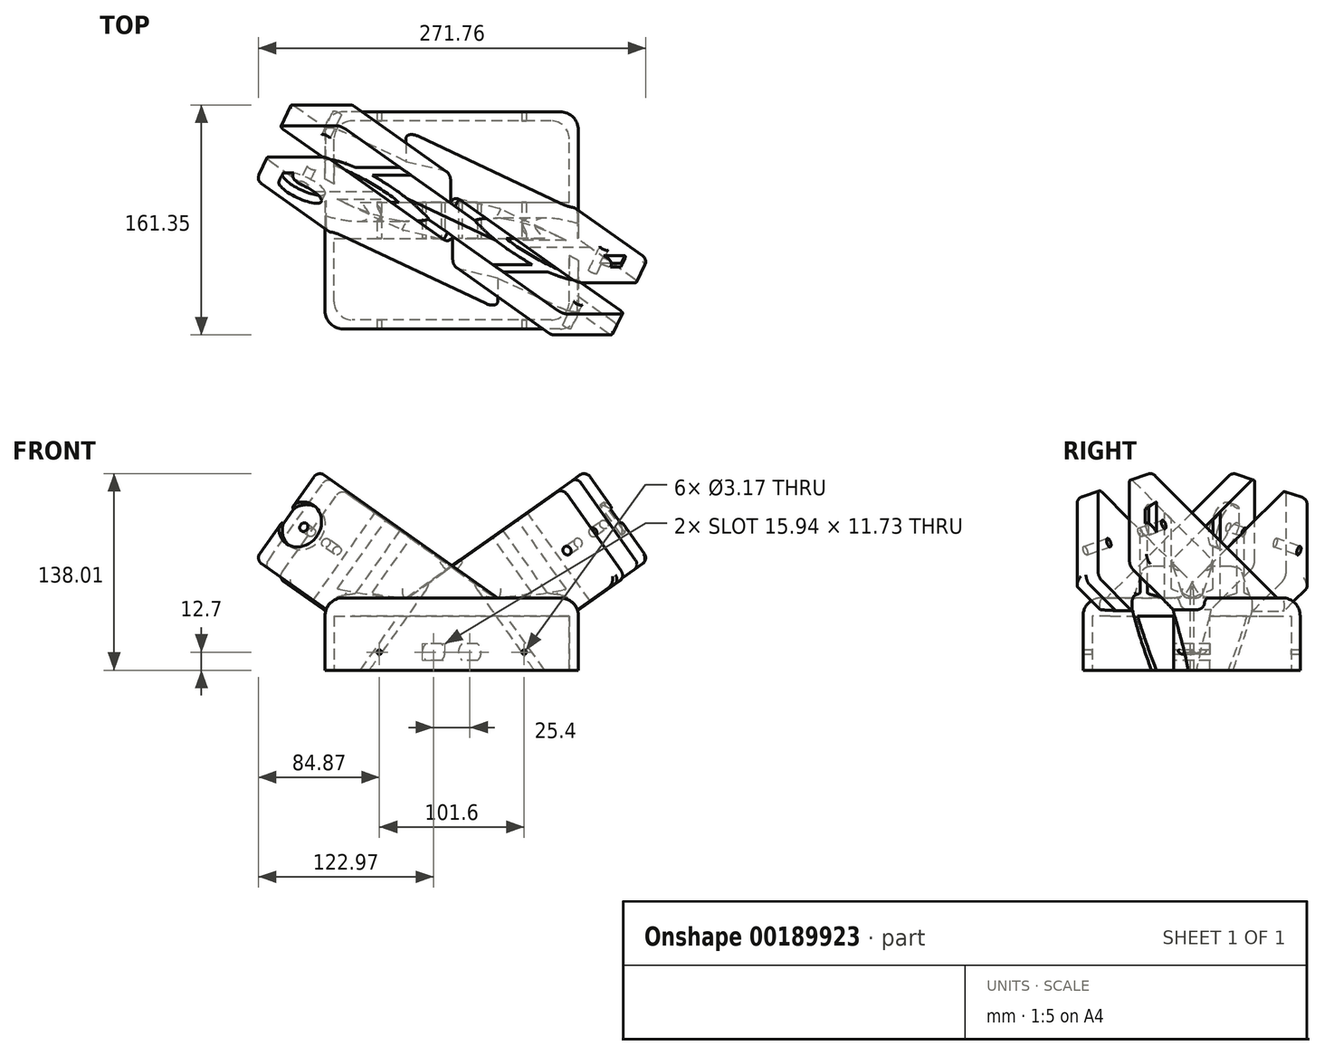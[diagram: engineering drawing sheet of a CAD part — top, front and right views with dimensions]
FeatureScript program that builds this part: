
annotation { "Feature Type Name" : "Feature", "Feature Type Description" : "" }
export const myFeature = defineFeature(function(context is Context, id is Id, definition is map)
    precondition{}
    {
        {
            var Q0;
            Q0=qCreatedBy(makeId("Top.planeOp"),FACE);
            var sketch = newSketch(context, id + "F0", { "sketchPlane" : qUnion([Q0])});
            skLineSegment(sketch, "E0.bottom", {"start": v(76.2, 73.97) * mm, "end": v(-76.2, 73.97) * mm});
            skLineSegment(sketch, "E0.top", {"start": v(76.2, -78.43) * mm, "end": v(-76.2, -78.43) * mm});
            skLineSegment(sketch, "E0.left", {"start": v(88.9, 61.27) * mm, "end": v(88.9, -65.73) * mm});
            skLineSegment(sketch, "E0.right", {"start": v(-88.9, 61.27) * mm, "end": v(-88.9, -65.73) * mm});
            skPoint(sketch, "E0.middle", {"position": v(0, -2.23) * mm});
            skPoint(sketch, "E1.visualSharp", {"position": v(-88.9, 73.97) * mm});
            skArc(sketch, "E1.filletArc", {"start": v(-76.2, 73.97) * mm, "mid": v(-85.18, 70.25) * mm, "end": v(-88.9, 61.27) * mm});
            skPoint(sketch, "E2.visualSharp", {"position": v(88.9, -78.43) * mm});
            skArc(sketch, "E2.filletArc", {"start": v(76.2, -78.43) * mm, "mid": v(85.18, -74.72) * mm, "end": v(88.9, -65.73) * mm});
            skPoint(sketch, "E3.visualSharp", {"position": v(88.9, 73.97) * mm});
            skArc(sketch, "E3.filletArc", {"start": v(88.9, 61.27) * mm, "mid": v(85.18, 70.25) * mm, "end": v(76.2, 73.97) * mm});
            skPoint(sketch, "E4.visualSharp", {"position": v(-88.9, -78.43) * mm});
            skArc(sketch, "E4.filletArc", {"start": v(-88.9, -65.73) * mm, "mid": v(-85.18, -74.72) * mm, "end": v(-76.2, -78.43) * mm});
            skSolve(sketch);
        }
        {
            var Q0;
            Q0 = qSketchRegion(id + "F0", true);
            extrude(context, id + "F1", {"entities" : qUnion([Q0]), "depth" : 50.8 * mm});
        }
        {
            var Q0;
            Q0=makeQuery(id+"F1.opExtrude","CAP_EDGE",EDGE,{"disambiguationData":[OSD([sQuery(id+"F0.wireOp",EDGE,"E0.bottom")])],"isStart":false});
            fillet(context, id + "F2", {"entities" : qUnion([Q0]), "radius" : 12.7 * mm, "tangentPropagation" : true, "allowEdgeOverflow" : false});
        }
        {
            var Q0;
            Q0=makeQuery(id+"F1.opExtrude","CAP_FACE",FACE,{"disambiguationData":[OSD([sQuery(id+"F0.wireOp",EDGE,"E0.bottom"),sQuery(id+"F0.wireOp",EDGE,"E0.top"),sQuery(id+"F0.wireOp",EDGE,"E0.left"),sQuery(id+"F0.wireOp",EDGE,"E0.right"),sQuery(id+"F0.wireOp",EDGE,"E1.filletArc"),sQuery(id+"F0.wireOp",EDGE,"E2.filletArc"),sQuery(id+"F0.wireOp",EDGE,"E3.filletArc"),sQuery(id+"F0.wireOp",EDGE,"E4.filletArc")])],"isStart":false});
            var Q1;
            Q1=makeQuery(id+"F1.opExtrude","SWEPT_FACE",FACE,{"disambiguationData":[OSD([sQuery(id+"F0.wireOp",EDGE,"E0.bottom")])]});
            cPlane(context, id + "F3", {"entities" : qUnion([Q0, Q1]), "cplaneType" : CPlaneType.MID_PLANE, "offset" : 25.4 * mm, "flipAlignment" : true, "width" : 152.4 * mm, "height" : 152.4 * mm});
        }
        {
            var Q0;
            Q0=qCreatedBy(id+"F3.planeOp",FACE);
            var Q1;
            Q1=makeQuery(id+"F1.opExtrude","SWEPT_FACE",FACE,{"disambiguationData":[OSD([sQuery(id+"F0.wireOp",EDGE,"E0.right")])]});
            cPlane(context, id + "F4", {"entities" : qUnion([Q0, Q1]), "cplaneType" : CPlaneType.MID_PLANE, "offset" : 25.4 * mm, "flipAlignment" : true, "width" : 152.4 * mm, "height" : 152.4 * mm});
        }
        {
            var Q0;
            Q0=qCreatedBy(id+"F4.planeOp",FACE);
            var sketch = newSketch(context, id + "F5", { "sketchPlane" : qUnion([Q0])});
            skLineSegment(sketch, "E5.bottom", {"start": v(-6.12, -17.18) * mm, "end": v(12.93, -17.18) * mm});
            skLineSegment(sketch, "E5.top", {"start": v(-6.12, 59.02) * mm, "end": v(12.93, 59.02) * mm});
            skLineSegment(sketch, "E5.left", {"start": v(-6.12, -17.18) * mm, "end": v(-6.12, 59.02) * mm});
            skLineSegment(sketch, "E5.right", {"start": v(12.93, -17.18) * mm, "end": v(12.93, 59.02) * mm});
            skLineSegment(sketch, "E6.bottom", {"start": v(57.38, -16) * mm, "end": v(38.33, -16) * mm});
            skLineSegment(sketch, "E6.top", {"start": v(57.38, 60.2) * mm, "end": v(38.33, 60.2) * mm});
            skLineSegment(sketch, "E6.left", {"start": v(57.38, -16) * mm, "end": v(57.38, 60.2) * mm});
            skLineSegment(sketch, "E6.right", {"start": v(38.33, -16) * mm, "end": v(38.33, 60.2) * mm});
            skSolve(sketch);
        }
        {
            var Q0;
            Q0=makeQuery(id+"F5.imprint","IMPRINT",FACE,{"disambiguationData":[TD([[makeQuery(id+"F5.imprint","IMPRINT",EDGE,{"derivedFrom":sQuery(id+"F5.wireOp",EDGE,"E6.bottom")}),-1.0]])]});
            var Q1;
            Q1=makeQuery(id+"F5.imprint","IMPRINT",FACE,{"disambiguationData":[TD([[makeQuery(id+"F5.imprint","IMPRINT",EDGE,{"derivedFrom":sQuery(id+"F5.wireOp",EDGE,"E5.bottom")}),1.0]])]});
            extrude(context, id + "F6", {"entities" : qUnion([Q0, Q1]), "operationType" : NewBodyOperationType.ADD, "depth" : 25.4 * mm, "hasSecondDirection" : true, "secondDirectionOppositeDirection" : true, "secondDirectionDepth" : 180.34 * mm});
        }
        {
            var Q0;
            Q0=makeQuery(id+"F1.opExtrude","SWEPT_FACE",FACE,{"disambiguationData":[OSD([sQuery(id+"F0.wireOp",EDGE,"E0.top")])]});
            var Q1;
            Q1=makeQuery(id+"F1.opExtrude","CAP_FACE",FACE,{"disambiguationData":[OSD([sQuery(id+"F0.wireOp",EDGE,"E0.bottom"),sQuery(id+"F0.wireOp",EDGE,"E0.top"),sQuery(id+"F0.wireOp",EDGE,"E0.left"),sQuery(id+"F0.wireOp",EDGE,"E0.right"),sQuery(id+"F0.wireOp",EDGE,"E1.filletArc"),sQuery(id+"F0.wireOp",EDGE,"E2.filletArc"),sQuery(id+"F0.wireOp",EDGE,"E3.filletArc"),sQuery(id+"F0.wireOp",EDGE,"E4.filletArc")])],"isStart":false});
            cPlane(context, id + "F7", {"entities" : qUnion([Q0, Q1]), "cplaneType" : CPlaneType.MID_PLANE, "offset" : 25.4 * mm, "flipAlignment" : true, "width" : 152.4 * mm, "height" : 152.4 * mm});
        }
        {
            var Q0;
            Q0=qCreatedBy(id+"F7.planeOp",FACE);
            var Q1;
            Q1=makeQuery(id+"F1.opExtrude","SWEPT_FACE",FACE,{"disambiguationData":[OSD([sQuery(id+"F0.wireOp",EDGE,"E0.left")])]});
            cPlane(context, id + "F8", {"entities" : qUnion([Q0, Q1]), "cplaneType" : CPlaneType.MID_PLANE, "offset" : 25.4 * mm, "flipAlignment" : true, "width" : 152.4 * mm, "height" : 152.4 * mm});
        }
        {
            var Q0;
            Q0=qCreatedBy(id+"F8.planeOp",FACE);
            var sketch = newSketch(context, id + "F9", { "sketchPlane" : qUnion([Q0])});
            skLineSegment(sketch, "E7.bottom", {"start": v(0, -16.82) * mm, "end": v(9.8, -16.82) * mm});
            skLineSegment(sketch, "E7.top", {"start": v(-9.25, 59.38) * mm, "end": v(9.8, 59.38) * mm});
            skLineSegment(sketch, "E7.left", {"start": v(-9.25, -16.23) * mm, "end": v(-9.25, 59.38) * mm});
            skLineSegment(sketch, "E7.right", {"start": v(9.8, -16.82) * mm, "end": v(9.8, 59.38) * mm});
            skLineSegment(sketch, "E8.bottom", {"start": v(35.2, -16.2) * mm, "end": v(54.25, -16.2) * mm});
            skLineSegment(sketch, "E8.top", {"start": v(35.2, 60) * mm, "end": v(54.25, 60) * mm});
            skLineSegment(sketch, "E8.left", {"start": v(35.2, -16.2) * mm, "end": v(35.2, 60) * mm});
            skLineSegment(sketch, "E8.right", {"start": v(54.25, -16.2) * mm, "end": v(54.25, 60) * mm});
            skLineSegment(sketch, "E9", {"start": v(-9.25, -16.23) * mm, "end": v(0, -16.82) * mm});
            skSolve(sketch);
        }
        {
            var Q0;
            Q0 = qSketchRegion(id + "F9", true);
            extrude(context, id + "F10", {"entities" : qUnion([Q0]), "operationType" : NewBodyOperationType.ADD, "depth" : 25.4 * mm, "hasSecondDirection" : true, "secondDirectionOppositeDirection" : true, "secondDirectionDepth" : 180.34 * mm});
        }
        {
            var Q0;
            Q0=makeQuery(id+"F1.opExtrude","SWEPT_FACE",FACE,{"disambiguationData":[OSD([sQuery(id+"F0.wireOp",EDGE,"E0.top")])]});
            var sketch = newSketch(context, id + "F11", { "sketchPlane" : qUnion([Q0])});
            skLineSegment(sketch, "E10.bottom", {"start": v(-76.2, 0) * mm, "end": v(127.6, 0) * mm});
            skLineSegment(sketch, "E10.top", {"start": v(-76.2, -80.49) * mm, "end": v(127.6, -80.49) * mm});
            skLineSegment(sketch, "E10.left", {"start": v(-76.2, 0) * mm, "end": v(-76.2, -80.49) * mm});
            skLineSegment(sketch, "E10.right", {"start": v(127.6, 0) * mm, "end": v(127.6, -80.49) * mm});
            skSolve(sketch);
        }
        {
            var Q0;
            Q0 = qSketchRegion(id + "F11", true);
            extrude(context, id + "F12", {"entities" : qUnion([Q0]), "operationType" : NewBodyOperationType.REMOVE, "endBound" : BoundingType.THROUGH_ALL, "oppositeDirection" : true, "depth" : 25.4 * mm});
        }
        {
            var Q0;
            Q0=makeQuery(id+"F12.boolean.opBoolean","MERGE",FACE,{"derivedFrom":[makeQuery(id+"F1.opExtrude","CAP_FACE",FACE,{"disambiguationData":[OSD([sQuery(id+"F0.wireOp",EDGE,"E0.bottom"),sQuery(id+"F0.wireOp",EDGE,"E0.top"),sQuery(id+"F0.wireOp",EDGE,"E0.left"),sQuery(id+"F0.wireOp",EDGE,"E0.right"),sQuery(id+"F0.wireOp",EDGE,"E1.filletArc"),sQuery(id+"F0.wireOp",EDGE,"E2.filletArc"),sQuery(id+"F0.wireOp",EDGE,"E3.filletArc"),sQuery(id+"F0.wireOp",EDGE,"E4.filletArc")])],"isStart":true}),makeQuery(id+"F12.opExtrude","SWEPT_FACE",FACE,{"disambiguationData":[OSD([sQuery(id+"F11.wireOp",EDGE,"E10.bottom")])]})]});
            var sketch = newSketch(context, id + "F13", { "sketchPlane" : qUnion([Q0])});
            skLineSegment(sketch, "E11.bottom", {"start": v(69.85, 72.08) * mm, "end": v(-69.85, 72.08) * mm});
            skLineSegment(sketch, "E11.top", {"start": v(69.85, -67.62) * mm, "end": v(-69.85, -67.62) * mm});
            skLineSegment(sketch, "E11.left", {"start": v(82.55, 59.38) * mm, "end": v(82.55, -54.92) * mm});
            skLineSegment(sketch, "E11.right", {"start": v(-82.55, 59.38) * mm, "end": v(-82.55, -54.92) * mm});
            skPoint(sketch, "E11.middle", {"position": v(0, 0) * mm});
            skPoint(sketch, "E12.visualSharp", {"position": v(-82.55, 72.08) * mm});
            skArc(sketch, "E12.filletArc", {"start": v(-69.85, 72.08) * mm, "mid": v(-78.83, 68.37) * mm, "end": v(-82.55, 59.38) * mm});
            skPoint(sketch, "E13.visualSharp", {"position": v(-82.55, -67.62) * mm});
            skArc(sketch, "E13.filletArc", {"start": v(-82.55, -54.92) * mm, "mid": v(-78.83, -63.9) * mm, "end": v(-69.85, -67.62) * mm});
            skPoint(sketch, "E14.visualSharp", {"position": v(82.55, -67.62) * mm});
            skArc(sketch, "E14.filletArc", {"start": v(69.85, -67.62) * mm, "mid": v(78.83, -63.9) * mm, "end": v(82.55, -54.92) * mm});
            skPoint(sketch, "E15.visualSharp", {"position": v(82.55, 72.08) * mm});
            skArc(sketch, "E15.filletArc", {"start": v(82.55, 59.38) * mm, "mid": v(78.83, 68.37) * mm, "end": v(69.85, 72.08) * mm});
            skLineSegment(sketch, "E16.bottom", {"start": v(-82.55, -10.47) * mm, "end": v(82.55, -10.47) * mm});
            skLineSegment(sketch, "E16.top", {"start": v(-82.55, 14.93) * mm, "end": v(82.55, 14.93) * mm});
            skLineSegment(sketch, "E16.left", {"start": v(-82.55, -10.47) * mm, "end": v(-82.55, 14.93) * mm});
            skLineSegment(sketch, "E16.right", {"start": v(82.55, -10.47) * mm, "end": v(82.55, 14.93) * mm});
            skSolve(sketch);
        }
        {
            var Q0;
            Q0=makeQuery(id+"F13.imprint","IMPRINT",FACE,{"disambiguationData":[TD([[makeQuery(id+"F13.imprint","IMPRINT",EDGE,{"derivedFrom":sQuery(id+"F13.wireOp",EDGE,"E11.bottom")}),1.0]])]});
            var Q1;
            Q1=makeQuery(id+"F13.imprint","IMPRINT",FACE,{"disambiguationData":[TD([[makeQuery(id+"F13.imprint","IMPRINT",EDGE,{"derivedFrom":sQuery(id+"F13.wireOp",EDGE,"E11.top")}),-1.0]])]});
            extrude(context, id + "F14", {"entities" : qUnion([Q0, Q1]), "operationType" : NewBodyOperationType.REMOVE, "oppositeDirection" : true, "depth" : 38.1 * mm});
        }
        {
            var Q0;
            Q0=makeQuery(id+"F10.opExtrude","CAP_EDGE",EDGE,{"disambiguationData":[OSD([sQuery(id+"F9.wireOp",EDGE,"E7.bottom")])],"isStart":false});
            var Q1;
            Q1=makeQuery(id+"F10.opExtrude","CAP_EDGE",EDGE,{"disambiguationData":[OSD([sQuery(id+"F9.wireOp",EDGE,"E7.top")])],"isStart":false});
            var Q2;
            Q2=makeQuery(id+"F10.opExtrude","CAP_EDGE",EDGE,{"disambiguationData":[OSD([sQuery(id+"F9.wireOp",EDGE,"E8.top")])],"isStart":false});
            var Q3;
            Q3=makeQuery(id+"F10.opExtrude","CAP_EDGE",EDGE,{"disambiguationData":[OSD([sQuery(id+"F9.wireOp",EDGE,"E8.bottom")])],"isStart":false});
            var Q4;
            Q4=makeQuery(id+"F10.opExtrude","CAP_EDGE",EDGE,{"disambiguationData":[OSD([sQuery(id+"F9.wireOp",EDGE,"E9")])],"isStart":false});
            var Q5;
            Q5=makeQuery(id+"F10.opExtrude","CAP_EDGE",EDGE,{"disambiguationData":[OSD([sQuery(id+"F9.wireOp",EDGE,"E7.left")])],"isStart":false});
            var Q6;
            Q6=makeQuery(id+"F10.opExtrude","CAP_EDGE",EDGE,{"disambiguationData":[OSD([sQuery(id+"F9.wireOp",EDGE,"E8.right")])],"isStart":false});
            var Q7;
            Q7=makeQuery(id+"F6.opExtrude","CAP_EDGE",EDGE,{"disambiguationData":[OSD([sQuery(id+"F5.wireOp",EDGE,"E6.left")])],"isStart":false});
            var Q8;
            Q8=makeQuery(id+"F6.opExtrude","CAP_EDGE",EDGE,{"disambiguationData":[OSD([sQuery(id+"F5.wireOp",EDGE,"E6.bottom")])],"isStart":false});
            var Q9;
            Q9=makeQuery(id+"F6.opExtrude","CAP_EDGE",EDGE,{"disambiguationData":[OSD([sQuery(id+"F5.wireOp",EDGE,"E6.top")])],"isStart":false});
            var Q10;
            Q10=makeQuery(id+"F6.opExtrude","CAP_EDGE",EDGE,{"disambiguationData":[OSD([sQuery(id+"F5.wireOp",EDGE,"E5.bottom")])],"isStart":false});
            var Q11;
            Q11=makeQuery(id+"F6.opExtrude","CAP_EDGE",EDGE,{"disambiguationData":[OSD([sQuery(id+"F5.wireOp",EDGE,"E5.left")])],"isStart":false});
            var Q12;
            Q12=makeQuery(id+"F6.opExtrude","CAP_EDGE",EDGE,{"disambiguationData":[OSD([sQuery(id+"F5.wireOp",EDGE,"E5.top")])],"isStart":false});
            var Q13;
            Q13=makeQuery(id+"F6.opExtrude","SWEPT_EDGE",EDGE,{"disambiguationData":[OSD([sQuery(id+"F5.wireOp",EDGE,"E5.top"),sQuery(id+"F5.wireOp",EDGE,"E5.left")])]});
            var Q14;
            Q14=makeQuery(id+"F6.opExtrude","SWEPT_EDGE",EDGE,{"disambiguationData":[OSD([sQuery(id+"F5.wireOp",EDGE,"E6.top"),sQuery(id+"F5.wireOp",EDGE,"E6.left")])]});
            var Q15;
            {var subQ0=sQuery(id+"F5.wireOp",EDGE,"E6.bottom");var subQ1=sQuery(id+"F5.wireOp",EDGE,"E6.left");Q15=makeQuery(id+"F6.boolean.opBoolean","SPLIT",EDGE,{"disambiguationData":[TD([makeQuery(id+"F6.opExtrude","CAP_FACE",FACE,{"disambiguationData":[OSD([subQ0,sQuery(id+"F5.wireOp",EDGE,"E6.top"),subQ1,sQuery(id+"F5.wireOp",EDGE,"E6.right")])],"isStart":false})])],"derivedFrom":makeQuery(id+"F6.opExtrude","SWEPT_EDGE",EDGE,{"disambiguationData":[OSD([subQ0,subQ1])]})});}
            var Q16;
            {var subQ0=sQuery(id+"F5.wireOp",EDGE,"E5.left");var subQ1=sQuery(id+"F5.wireOp",EDGE,"E5.bottom");Q16=makeQuery(id+"F6.boolean.opBoolean","SPLIT",EDGE,{"disambiguationData":[TD([makeQuery(id+"F2.opFillet","BLEND_FACE",FACE,{"disambiguationData":[OSD([sQuery(id+"F0.wireOp",EDGE,"E0.bottom")])]})])],"derivedFrom":makeQuery(id+"F6.opExtrude","SWEPT_EDGE",EDGE,{"disambiguationData":[OSD([subQ1,subQ0])]})});}
            var Q17;
            Q17=makeQuery(id+"F10.opExtrude","SWEPT_EDGE",EDGE,{"disambiguationData":[OSD([sQuery(id+"F9.wireOp",EDGE,"E8.top"),sQuery(id+"F9.wireOp",EDGE,"E8.right")])]});
            var Q18;
            Q18=makeQuery(id+"F10.opExtrude","SWEPT_EDGE",EDGE,{"disambiguationData":[OSD([sQuery(id+"F9.wireOp",EDGE,"E7.top"),sQuery(id+"F9.wireOp",EDGE,"E7.left")])]});
            var Q19;
            {var subQ0=sQuery(id+"F9.wireOp",EDGE,"E7.left");var subQ1=sQuery(id+"F9.wireOp",EDGE,"E9");Q19=makeQuery(id+"F10.boolean.opBoolean","SPLIT",EDGE,{"disambiguationData":[TD([makeQuery(id+"F2.opFillet","BLEND_FACE",FACE,{"disambiguationData":[OSD([sQuery(id+"F0.wireOp",EDGE,"E0.top")])]})])],"derivedFrom":makeQuery(id+"F10.opExtrude","SWEPT_EDGE",EDGE,{"disambiguationData":[OSD([subQ0,subQ1])]})});}
            var Q20;
            {var subQ0=sQuery(id+"F9.wireOp",EDGE,"E8.bottom");var subQ1=sQuery(id+"F9.wireOp",EDGE,"E8.right");Q20=makeQuery(id+"F10.boolean.opBoolean","SPLIT",EDGE,{"disambiguationData":[TD([makeQuery(id+"F10.opExtrude","CAP_FACE",FACE,{"disambiguationData":[OSD([subQ0,sQuery(id+"F9.wireOp",EDGE,"E8.top"),sQuery(id+"F9.wireOp",EDGE,"E8.left"),subQ1])],"isStart":false})])],"derivedFrom":makeQuery(id+"F10.opExtrude","SWEPT_EDGE",EDGE,{"disambiguationData":[OSD([subQ0,subQ1])]})});}
            fillet(context, id + "F15", {"entities" : qUnion([Q0, Q1, Q2, Q3, Q4, Q5, Q6, Q7, Q8, Q9, Q10, Q11, Q12, Q13, Q14, Q15, Q16, Q17, Q18, Q19, Q20]), "radius" : 5.08 * mm, "tangentPropagation" : true, "allowEdgeOverflow" : false});
        }
        {
            var Q0;
            {var subQ1=sQuery(id+"F9.wireOp",EDGE,"E8.right");var subQ2=sQuery(id+"F9.wireOp",EDGE,"E8.top");Q0=makeQuery(id+"F10.boolean.opBoolean","SPLIT",FACE,{"disambiguationData":[TD([makeQuery(id+"F10.opExtrude","SWEPT_FACE",FACE,{"disambiguationData":[OSD([subQ2])]})])],"derivedFrom":makeQuery(id+"F10.opExtrude","SWEPT_FACE",FACE,{"disambiguationData":[OSD([subQ1])]})});}
            var sketch = newSketch(context, id + "F16", { "sketchPlane" : qUnion([Q0])});
            skCircle(sketch, "E17", {"center": v(-92.77, 104) * mm, "radius": 3.18 * mm});
            skLineSegment(sketch, "E18", {"start": v(-100.64, 110.44) * mm, "end": v(-61.64, 78.6) * mm, "construction": true});
            skSolve(sketch);
        }
        {
            var Q0;
            Q0 = qSketchRegion(id + "F16", true);
            extrude(context, id + "F17", {"entities" : qUnion([Q0]), "operationType" : NewBodyOperationType.REMOVE, "endBound" : BoundingType.THROUGH_ALL, "oppositeDirection" : true, "depth" : 25.4 * mm});
        }
        {
            var Q0;
            {var subQ1=sQuery(id+"F5.wireOp",EDGE,"E6.left");var subQ2=sQuery(id+"F5.wireOp",EDGE,"E6.top");Q0=makeQuery(id+"F6.boolean.opBoolean","SPLIT",FACE,{"disambiguationData":[TD([makeQuery(id+"F6.opExtrude","SWEPT_FACE",FACE,{"disambiguationData":[OSD([subQ2])]})])],"derivedFrom":makeQuery(id+"F6.opExtrude","SWEPT_FACE",FACE,{"disambiguationData":[OSD([subQ1])]})});}
            var sketch = newSketch(context, id + "F18", { "sketchPlane" : qUnion([Q0])});
            skLineSegment(sketch, "E19", {"start": v(-98.78, 109.18) * mm, "end": v(-95.73, 106.7) * mm, "construction": true});
            skCircle(sketch, "E20", {"center": v(-90.9, 102.76) * mm, "radius": 3.18 * mm});
            skSolve(sketch);
        }
        {
            var Q0;
            Q0=makeQuery(id+"F18.imprint","IMPRINT",FACE,{"disambiguationData":[TD([[makeQuery(id+"F18.imprint","IMPRINT",EDGE,{"derivedFrom":sQuery(id+"F18.wireOp",EDGE,"E20")}),1.0]])]});
            extrude(context, id + "F19", {"entities" : qUnion([Q0]), "operationType" : NewBodyOperationType.REMOVE, "endBound" : BoundingType.THROUGH_ALL, "oppositeDirection" : true, "depth" : 25.4 * mm});
        }
        {
            var Q0;
            Q0=makeQuery(id+"F6.boolean.opBoolean","INTERSECT",EDGE,{"derivedFrom":[makeQuery(id+"F1.opExtrude","CAP_FACE",FACE,{"disambiguationData":[OSD([sQuery(id+"F0.wireOp",EDGE,"E0.bottom"),sQuery(id+"F0.wireOp",EDGE,"E0.top"),sQuery(id+"F0.wireOp",EDGE,"E0.left"),sQuery(id+"F0.wireOp",EDGE,"E0.right"),sQuery(id+"F0.wireOp",EDGE,"E1.filletArc"),sQuery(id+"F0.wireOp",EDGE,"E2.filletArc"),sQuery(id+"F0.wireOp",EDGE,"E3.filletArc"),sQuery(id+"F0.wireOp",EDGE,"E4.filletArc")])],"isStart":false}),makeQuery(id+"F6.opExtrude","SWEPT_FACE",FACE,{"disambiguationData":[OSD([sQuery(id+"F5.wireOp",EDGE,"E5.right")])]})]});
            var Q1;
            Q1=makeQuery(id+"F6.boolean.opBoolean","INTERSECT",EDGE,{"derivedFrom":[makeQuery(id+"F1.opExtrude","CAP_FACE",FACE,{"disambiguationData":[OSD([sQuery(id+"F0.wireOp",EDGE,"E0.bottom"),sQuery(id+"F0.wireOp",EDGE,"E0.top"),sQuery(id+"F0.wireOp",EDGE,"E0.left"),sQuery(id+"F0.wireOp",EDGE,"E0.right"),sQuery(id+"F0.wireOp",EDGE,"E1.filletArc"),sQuery(id+"F0.wireOp",EDGE,"E2.filletArc"),sQuery(id+"F0.wireOp",EDGE,"E3.filletArc"),sQuery(id+"F0.wireOp",EDGE,"E4.filletArc")])],"isStart":false}),makeQuery(id+"F6.opExtrude","SWEPT_FACE",FACE,{"disambiguationData":[OSD([sQuery(id+"F5.wireOp",EDGE,"E6.right")])]})]});
            fillet(context, id + "F20", {"entities" : qUnion([Q0, Q1]), "radius" : 5.08 * mm, "tangentPropagation" : true, "allowEdgeOverflow" : false});
        }
        {
            var Q0;
            Q0=makeQuery(id+"F10.boolean.opBoolean","INTERSECT",EDGE,{"derivedFrom":[makeQuery(id+"F1.opExtrude","CAP_FACE",FACE,{"disambiguationData":[OSD([sQuery(id+"F0.wireOp",EDGE,"E0.bottom"),sQuery(id+"F0.wireOp",EDGE,"E0.top"),sQuery(id+"F0.wireOp",EDGE,"E0.left"),sQuery(id+"F0.wireOp",EDGE,"E0.right"),sQuery(id+"F0.wireOp",EDGE,"E1.filletArc"),sQuery(id+"F0.wireOp",EDGE,"E2.filletArc"),sQuery(id+"F0.wireOp",EDGE,"E3.filletArc"),sQuery(id+"F0.wireOp",EDGE,"E4.filletArc")])],"isStart":false}),makeQuery(id+"F10.opExtrude","SWEPT_FACE",FACE,{"disambiguationData":[OSD([sQuery(id+"F9.wireOp",EDGE,"E7.right")])]})]});
            var Q1;
            Q1=makeQuery(id+"F10.boolean.opBoolean","INTERSECT",EDGE,{"derivedFrom":[makeQuery(id+"F1.opExtrude","CAP_FACE",FACE,{"disambiguationData":[OSD([sQuery(id+"F0.wireOp",EDGE,"E0.bottom"),sQuery(id+"F0.wireOp",EDGE,"E0.top"),sQuery(id+"F0.wireOp",EDGE,"E0.left"),sQuery(id+"F0.wireOp",EDGE,"E0.right"),sQuery(id+"F0.wireOp",EDGE,"E1.filletArc"),sQuery(id+"F0.wireOp",EDGE,"E2.filletArc"),sQuery(id+"F0.wireOp",EDGE,"E3.filletArc"),sQuery(id+"F0.wireOp",EDGE,"E4.filletArc")])],"isStart":false}),makeQuery(id+"F10.opExtrude","SWEPT_FACE",FACE,{"disambiguationData":[OSD([sQuery(id+"F9.wireOp",EDGE,"E8.left")])]})]});
            fillet(context, id + "F21", {"entities" : qUnion([Q0, Q1]), "radius" : 5.08 * mm, "tangentPropagation" : true, "allowEdgeOverflow" : false});
        }
        {
            var Q0;
            Q0=makeQuery(id+"F6.boolean.opBoolean","INTERSECT",EDGE,{"derivedFrom":[makeQuery(id+"F1.opExtrude","CAP_FACE",FACE,{"disambiguationData":[OSD([sQuery(id+"F0.wireOp",EDGE,"E0.bottom"),sQuery(id+"F0.wireOp",EDGE,"E0.top"),sQuery(id+"F0.wireOp",EDGE,"E0.left"),sQuery(id+"F0.wireOp",EDGE,"E0.right"),sQuery(id+"F0.wireOp",EDGE,"E1.filletArc"),sQuery(id+"F0.wireOp",EDGE,"E2.filletArc"),sQuery(id+"F0.wireOp",EDGE,"E3.filletArc"),sQuery(id+"F0.wireOp",EDGE,"E4.filletArc")])],"isStart":false}),makeQuery(id+"F6.opExtrude","SWEPT_FACE",FACE,{"disambiguationData":[OSD([sQuery(id+"F5.wireOp",EDGE,"E5.top")])]})]});
            var Q1;
            Q1=makeQuery(id+"F10.boolean.opBoolean","INTERSECT",EDGE,{"derivedFrom":[makeQuery(id+"F1.opExtrude","CAP_FACE",FACE,{"disambiguationData":[OSD([sQuery(id+"F0.wireOp",EDGE,"E0.bottom"),sQuery(id+"F0.wireOp",EDGE,"E0.top"),sQuery(id+"F0.wireOp",EDGE,"E0.left"),sQuery(id+"F0.wireOp",EDGE,"E0.right"),sQuery(id+"F0.wireOp",EDGE,"E1.filletArc"),sQuery(id+"F0.wireOp",EDGE,"E2.filletArc"),sQuery(id+"F0.wireOp",EDGE,"E3.filletArc"),sQuery(id+"F0.wireOp",EDGE,"E4.filletArc")])],"isStart":false}),makeQuery(id+"F10.opExtrude","SWEPT_FACE",FACE,{"disambiguationData":[OSD([sQuery(id+"F9.wireOp",EDGE,"E7.top")])]})]});
            fillet(context, id + "F22", {"entities" : qUnion([Q0, Q1]), "radius" : 5.08 * mm, "tangentPropagation" : true, "allowEdgeOverflow" : false});
        }
        {
            var Q0;
            Q0=makeQuery(id+"F1.opExtrude","SWEPT_FACE",FACE,{"disambiguationData":[OSD([sQuery(id+"F0.wireOp",EDGE,"E0.top")])]});
            var sketch = newSketch(context, id + "F23", { "sketchPlane" : qUnion([Q0])});
            skCircle(sketch, "E21", {"center": v(-50.8, 12.7) * mm, "radius": 1.59 * mm});
            skCircle(sketch, "E22", {"center": v(50.8, 12.7) * mm, "radius": 1.59 * mm});
            skSolve(sketch);
        }
        {
            var Q0;
            Q0 = qSketchRegion(id + "F23", true);
            extrude(context, id + "F24", {"entities" : qUnion([Q0]), "operationType" : NewBodyOperationType.REMOVE, "endBound" : BoundingType.THROUGH_ALL, "oppositeDirection" : true, "depth" : 25.4 * mm});
        }
        {
            var Q0;
            Q0=makeQuery(id+"F14.boolean.opBoolean","COPY",FACE,{"derivedFrom":makeQuery(id+"F14.opExtrude","SWEPT_FACE",FACE,{"disambiguationData":[OSD([sQuery(id+"F13.wireOp",EDGE,"E16.top")])]})});
            cPlane(context, id + "F25", {"entities" : qUnion([Q0]), "cplaneType" : CPlaneType.OFFSET, "offset" : 25.4 * mm, "width" : 152.4 * mm, "height" : 152.4 * mm});
        }
        {
            var Q0;
            Q0=qCreatedBy(id+"F25.planeOp",FACE);
            var sketch = newSketch(context, id + "F26", { "sketchPlane" : qUnion([Q0])});
            skArc(sketch, "E23", {"start": v(-7.3, 6.83) * mm, "mid": v(-4.73, 12.7) * mm, "end": v(-7.3, 18.57) * mm});
            skLineSegment(sketch, "E24", {"start": v(-18.1, 18.57) * mm, "end": v(-7.3, 18.57) * mm});
            skLineSegment(sketch, "E25", {"start": v(-18.1, 6.83) * mm, "end": v(-7.3, 6.83) * mm});
            skArc(sketch, "E26.trimOffspring", {"start": v(-18.1, 18.57) * mm, "mid": v(-20.67, 12.7) * mm, "end": v(-18.1, 6.83) * mm});
            skArc(sketch, "E27", {"start": v(18.1, 6.83) * mm, "mid": v(20.67, 12.7) * mm, "end": v(18.1, 18.57) * mm});
            skLineSegment(sketch, "E28", {"start": v(7.3, 18.57) * mm, "end": v(18.1, 18.57) * mm});
            skLineSegment(sketch, "E29", {"start": v(7.3, 6.83) * mm, "end": v(18.1, 6.83) * mm});
            skArc(sketch, "E30.trimOffspring", {"start": v(7.3, 18.57) * mm, "mid": v(4.73, 12.7) * mm, "end": v(7.3, 6.83) * mm});
            skSolve(sketch);
        }
        {
            var Q0;
            {var subQ0=sQuery(id+"F26.wireOp",EDGE,"E24");Q0=makeQuery(id+"F26.imprint","IMPRINT",FACE,{"disambiguationData":[TD([[makeQuery(id+"F26.imprint","IMPRINT",EDGE,{"derivedFrom":subQ0}),-1.0]])]});}
            var Q1;
            Q1=makeQuery(id+"F26.imprint","IMPRINT",FACE,{"disambiguationData":[TD([[makeQuery(id+"F26.imprint","IMPRINT",EDGE,{"derivedFrom":sQuery(id+"F26.wireOp",EDGE,"E27")}),1.0]])]});
            var Q2;
            Q2=makeQuery(id+"F14.boolean.opBoolean","COPY",FACE,{"derivedFrom":makeQuery(id+"F14.opExtrude","SWEPT_FACE",FACE,{"disambiguationData":[OSD([sQuery(id+"F13.wireOp",EDGE,"E11.top")])]})});
            extrude(context, id + "F27", {"entities" : qUnion([Q0, Q1]), "operationType" : NewBodyOperationType.REMOVE, "endBound" : BoundingType.UP_TO_SURFACE, "oppositeDirection" : true, "endBoundEntityFace" : qUnion([Q2]), "depth" : 25.4 * mm});
        }
        {
            var Q0;
            Q0=makeQuery(id+"F22.opFillet","SPLIT",FACE,{"disambiguationData":[OD(0.0)],"derivedFrom":makeQuery(id+"F10.opExtrude","SWEPT_FACE",FACE,{"disambiguationData":[OSD([sQuery(id+"F9.wireOp",EDGE,"E7.top")])]})});
            var Q1;
            Q1=makeQuery(id+"F10.opExtrude","SWEPT_FACE",FACE,{"disambiguationData":[OSD([sQuery(id+"F9.wireOp",EDGE,"E8.top")])]});
            cPlane(context, id + "F28", {"entities" : qUnion([Q0, Q1]), "cplaneType" : CPlaneType.MID_PLANE, "offset" : 25.4 * mm, "width" : 152.4 * mm, "height" : 152.4 * mm});
        }
        {
            var Q0;
            Q0=qCreatedBy(id+"F28.planeOp",FACE);
            var sketch = newSketch(context, id + "F29", { "sketchPlane" : qUnion([Q0])});
            skLineSegment(sketch, "E31", {"start": v(149.45, -45.64) * mm, "end": v(47.98, 12.94) * mm, "construction": true});
            skLineSegment(sketch, "E32", {"start": v(98.71, -16.35) * mm, "end": v(86.01, -38.35) * mm, "construction": true});
            skEllipse(sketch, "E33", {"center": v(92.36, -27.35) * mm, "majorRadius": 50.8 * mm, "minorRadius": 12.7 * mm, "majorAxis": v(0.88, -0.48)});
            skSolve(sketch);
        }
        {
            var Q0;
            Q0 = qSketchRegion(id + "F29", true);
            extrude(context, id + "F30", {"entities" : qUnion([Q0]), "operationType" : NewBodyOperationType.REMOVE, "endBound" : BoundingType.THROUGH_ALL, "oppositeDirection" : true, "depth" : 25.4 * mm});
        }
        {
            var Q0;
            Q0=makeQuery(id+"F22.opFillet","SPLIT",FACE,{"disambiguationData":[OD(0.0)],"derivedFrom":makeQuery(id+"F6.opExtrude","SWEPT_FACE",FACE,{"disambiguationData":[OSD([sQuery(id+"F5.wireOp",EDGE,"E5.top")])]})});
            var Q1;
            Q1=makeQuery(id+"F6.opExtrude","SWEPT_FACE",FACE,{"disambiguationData":[OSD([sQuery(id+"F5.wireOp",EDGE,"E6.top")])]});
            cPlane(context, id + "F31", {"entities" : qUnion([Q0, Q1]), "cplaneType" : CPlaneType.MID_PLANE, "offset" : 25.4 * mm, "width" : 152.4 * mm, "height" : 152.4 * mm});
        }
        {
            var Q0;
            Q0=qCreatedBy(id+"F31.planeOp",FACE);
            var sketch = newSketch(context, id + "F32", { "sketchPlane" : qUnion([Q0])});
            skLineSegment(sketch, "E34", {"start": v(-149.16, 41.85) * mm, "end": v(-48.24, -16.41) * mm, "construction": true});
            skLineSegment(sketch, "E35", {"start": v(-98.7, 12.72) * mm, "end": v(-86, 34.72) * mm, "construction": true});
            skEllipse(sketch, "E36", {"center": v(-92.35, 23.72) * mm, "majorRadius": 50.8 * mm, "minorRadius": 12.7 * mm, "majorAxis": v(-0.88, 0.48)});
            skSolve(sketch);
        }
        {
            var Q0;
            Q0 = qSketchRegion(id + "F32", true);
            extrude(context, id + "F33", {"entities" : qUnion([Q0]), "operationType" : NewBodyOperationType.REMOVE, "endBound" : BoundingType.THROUGH_ALL, "oppositeDirection" : true, "depth" : 25.4 * mm});
        }
        {
            var Q0;
            {var subQ0=sQuery(id+"F9.wireOp",EDGE,"E8.right");var subQ3=sQuery(id+"F0.wireOp",EDGE,"E0.left");Q0=makeQuery(id+"F10.boolean.opBoolean","SPLIT",FACE,{"disambiguationData":[TD([makeQuery(id+"F2.opFillet","BLEND_FACE",FACE,{"disambiguationData":[OSD([subQ3])]})])],"derivedFrom":makeQuery(id+"F10.opExtrude","SWEPT_FACE",FACE,{"disambiguationData":[OSD([subQ0])]})});}
            var sketch = newSketch(context, id + "F34", { "sketchPlane" : qUnion([Q0])});
            skCircle(sketch, "E37", {"center": v(-92.77, 104) * mm, "radius": 16.51 * mm});
            skSolve(sketch);
        }
        {
            var Q0;
            Q0=makeQuery(id+"F34.imprint","IMPRINT",FACE,{"disambiguationData":[TD([[makeQuery(id+"F34.imprint","IMPRINT",EDGE,{"derivedFrom":makeQuery(id+"F17.boolean.opBoolean","COPY",EDGE,{"derivedFrom":makeQuery(id+"F17.opExtrude","CAP_EDGE",EDGE,{"disambiguationData":[OSD([sQuery(id+"F16.wireOp",EDGE,"E17")])],"isStart":true})})}),-1.0]])]});
            var Q1;
            {var subQ0=sQuery(id+"F34.wireOp",EDGE,"E37");var subQ1=sQuery(id+"F9.wireOp",EDGE,"E8.right");var subQ4=sQuery(id+"F0.wireOp",EDGE,"E0.left");var subQ5=makeQuery(id+"F15.opFillet","BLEND_EDGE",EDGE,{"blendedFrom":[makeQuery(id+"F10.opExtrude","CAP_EDGE",EDGE,{"disambiguationData":[OSD([subQ1])],"isStart":false}),makeQuery(id+"F10.boolean.opBoolean","SPLIT",FACE,{"disambiguationData":[TD([makeQuery(id+"F2.opFillet","BLEND_FACE",FACE,{"disambiguationData":[OSD([subQ4])]})])],"derivedFrom":makeQuery(id+"F10.opExtrude","SWEPT_FACE",FACE,{"disambiguationData":[OSD([subQ1])]})})],"blendedInto":[makeQuery(id+"F10.boolean.opBoolean","SPLIT",FACE,{"disambiguationData":[TD([makeQuery(id+"F2.opFillet","BLEND_FACE",FACE,{"disambiguationData":[OSD([subQ4])]})])],"derivedFrom":makeQuery(id+"F10.opExtrude","SWEPT_FACE",FACE,{"disambiguationData":[OSD([subQ1])]})})]});var subQ6=makeQuery(id+"F34.imprint","INTERSECT",VERTEX,{"disambiguationData":[OD(0.0)],"derivedFrom":[subQ5,subQ0]});Q1=makeQuery(id+"F34.imprint","IMPRINT",FACE,{"disambiguationData":[TD([[makeQuery(id+"F34.imprint","IMPRINT",EDGE,{"disambiguationData":[TD([[subQ6,1.0]])],"derivedFrom":subQ0}),1.0]])]});}
            extrude(context, id + "F35", {"entities" : qUnion([Q0, Q1]), "operationType" : NewBodyOperationType.REMOVE, "oppositeDirection" : true, "depth" : 6.35 * mm});
        }
        {
            var Q0;
            {var subQ0=sQuery(id+"F5.wireOp",EDGE,"E6.left");var subQ3=sQuery(id+"F0.wireOp",EDGE,"E0.right");Q0=makeQuery(id+"F6.boolean.opBoolean","SPLIT",FACE,{"disambiguationData":[TD([makeQuery(id+"F2.opFillet","BLEND_FACE",FACE,{"disambiguationData":[OSD([subQ3])]})])],"derivedFrom":makeQuery(id+"F6.opExtrude","SWEPT_FACE",FACE,{"disambiguationData":[OSD([subQ0])]})});}
            var sketch = newSketch(context, id + "F36", { "sketchPlane" : qUnion([Q0])});
            skCircle(sketch, "E38", {"center": v(-90.9, 102.76) * mm, "radius": 16.51 * mm});
            skSolve(sketch);
        }
        {
            var Q0;
            Q0 = qSketchRegion(id + "F36", true);
            extrude(context, id + "F37", {"entities" : qUnion([Q0]), "operationType" : NewBodyOperationType.REMOVE, "oppositeDirection" : true, "depth" : 6.35 * mm});
        }
    });
